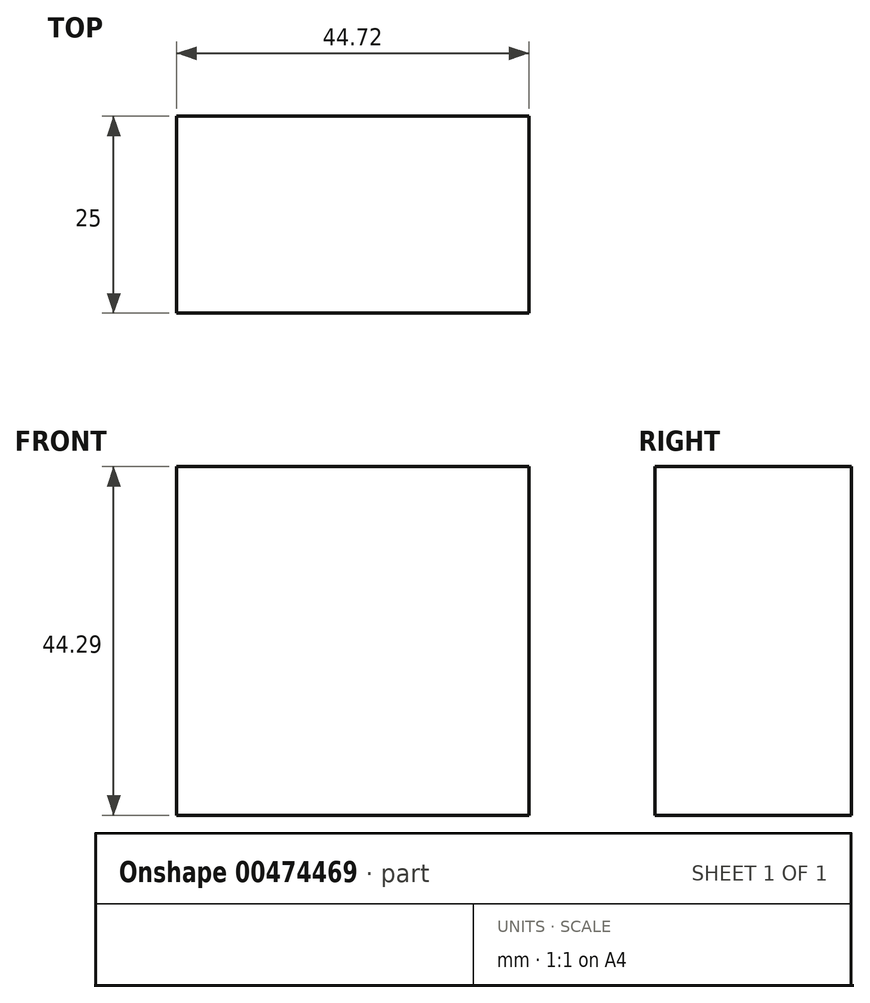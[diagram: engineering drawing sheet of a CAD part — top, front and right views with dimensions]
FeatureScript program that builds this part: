
annotation { "Feature Type Name" : "Feature", "Feature Type Description" : "" }
export const myFeature = defineFeature(function(context is Context, id is Id, definition is map)
    precondition{}
    {
        {
            var Q0;
            Q0=qCreatedBy(makeId("Front.planeOp"),FACE);
            var sketch = newSketch(context, id + "F0", { "sketchPlane" : qUnion([Q0])});
            skLineSegment(sketch, "E0.bottom", {"start": v(-78.77, 34.34) * mm, "end": v(-34.05, 34.34) * mm});
            skLineSegment(sketch, "E0.top", {"start": v(-78.77, 78.63) * mm, "end": v(-34.05, 78.63) * mm});
            skLineSegment(sketch, "E0.left", {"start": v(-78.77, 34.34) * mm, "end": v(-78.77, 78.63) * mm});
            skLineSegment(sketch, "E0.right", {"start": v(-34.05, 34.34) * mm, "end": v(-34.05, 78.63) * mm});
            skPoint(sketch, "E0.middle", {"position": v(-56.41, 56.48) * mm});
            skSolve(sketch);
        }
        {
            var Q0;
            Q0=makeQuery(id+"F0.imprint","IMPRINT",FACE,{"disambiguationData":[TD([[makeQuery(id+"F0.imprint","IMPRINT",EDGE,{"derivedFrom":sQuery(id+"F0.wireOp",EDGE,"E0.bottom")}),1.0]])]});
            extrude(context, id + "F1", {"entities" : qUnion([Q0]), "depth" : 25 * mm});
        }
    });
